# Revit family: Foundation-Barrier-Drago-Wrap-Vapor-Intrusion_Barrier
name_source: partatom
category: Specialty Equipment
units: mm (PartAtom-declared; Revit-internal decimal feet)

## family parameters
Cut with Voids When Loaded = No
Host = Face
OmniClass Number = 23.25.05.21
OmniClass Title = Special Foundations
Part Type = Normal
Room Calculation Point = No
Round Connector Dimension = Use Diameter
Shared = No

## types (1)
- Drago® Wrap Vapor Intrusion Barrier 20 mils
    ASTM = Meets ASTM E1745 Requirements.
    BIMobject category = Waterproofing & Membranes
    Brand url = http://www.stegoindustries.com
    Date of publishing = 3/27/2020
    Default Elevation = 0' - 0"
    Description = Drago Wrap is specifically engineered to serve as a barrier to volatile organic compounds (VOCs). Through patented and trade secret processes, Drago Wrap combines uniquely designed barrier materials with the flexibility and strength of a high-performance polyolefin film into an easy-to-install barrier against hydrocarbons and chlorinated solvents. It provides Owners, Developers, and Engineers a high-performing solution to transform brownfield sites into healthy built environments.
    Design country = United States
    Edition number = 1
    Installation instructions = https://www.stegoindustries.com

https://www.stegoindustries.com
https://www.stegoindustries.com
    Low Emitting Material = Yes
    Manufacturer = Stego Industries, LLC
    Manufacturer country = United States
    Manufacturer name = Stego Industries, LLC
    Masterformat 2014 Description = Vapor Retarder
    Material main = Polyethylene
    Max Length Note = Maximum roll length is 105'.
    Model = Drago® Wrap Vapor & Intrusion Barrier
    Nominal height = 0' - 0"
    Nominal width = 0' - 0"
    Product Documentation Link = https://www.stegoindustries.com
    Product Guid = https://www.stegoindustries.com
    Product Page URL = https://www.stegoindustries.com
    Product SKU = stego009
    Product certification = https://www.stegoindustries.com
    Product data url = https://bimobject.com
    Product family = Thermal and Moisture Protective Products
Thermal and Moisture Protective Products
Thermal and Moisture Protective Products
    Product group = Drago Wrap Vapor Intrusion Barrier
    Product url = https://www.stegoindustries.com

https://www.stegoindustries.com
https://www.stegoindustries.com
    QR code = https://bimobject.com
    Stego Vapor Barrier = Drago® Wrap Vapor Intrusion Barrier
    Technical description = Drago Wrap is specifically engineered to serve as a barrier to volatile organic compounds (VOCs).
    URL = http://www.stegoindustries.com
    Vapor Barrier Thickness = 20 mils
    Weight Net (Kg) = 0
    Youtube clip = https://youtu.be

## geometry (parser evidence)
native form markers: Sweep x2
no freeform markers — native parametric forms only
